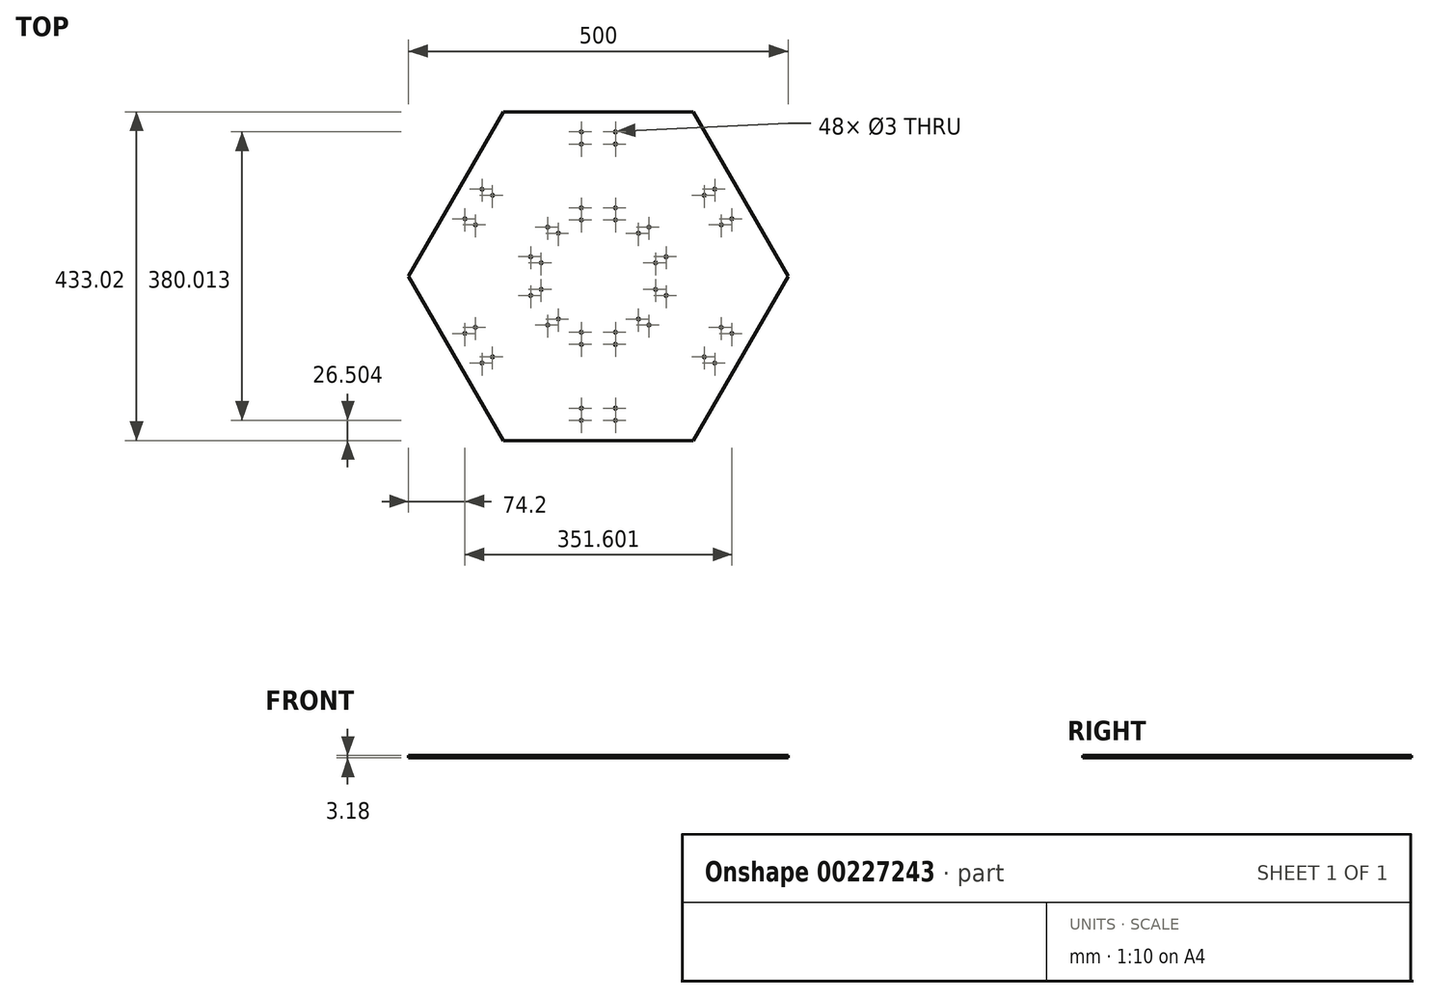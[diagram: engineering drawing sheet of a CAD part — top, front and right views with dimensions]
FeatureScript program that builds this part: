
annotation { "Feature Type Name" : "Feature", "Feature Type Description" : "" }
export const myFeature = defineFeature(function(context is Context, id is Id, definition is map)
    precondition{}
    {
        {
            var Q0;
            Q0=qCreatedBy(makeId("Top.planeOp"),FACE);
            var sketch = newSketch(context, id + "F0", { "sketchPlane" : qUnion([Q0])});
            skCircle(sketch, "E0.cCircle", {"center": v(0, 0) * mm, "radius": 250 * mm, "construction": true});
            skLineSegment(sketch, "E0.0", {"start": v(250, 0) * mm, "end": v(125, -216.5) * mm});
            skLineSegment(sketch, "E0.1", {"start": v(125, -216.5) * mm, "end": v(-125, -216.5) * mm});
            skLineSegment(sketch, "E0.2", {"start": v(-125, -216.5) * mm, "end": v(-250, 0) * mm});
            skLineSegment(sketch, "E0.3", {"start": v(-250, 0) * mm, "end": v(-125, 216.5) * mm});
            skLineSegment(sketch, "E0.4", {"start": v(-125, 216.5) * mm, "end": v(125, 216.5) * mm});
            skLineSegment(sketch, "E0.5", {"start": v(125, 216.5) * mm, "end": v(250, 0) * mm});
            skCircle(sketch, "E1", {"center": v(-22.5, 190) * mm, "radius": 1.5 * mm});
            skCircle(sketch, "E2.MirrorC", {"center": v(22.5, 190) * mm, "radius": 1.5 * mm});
            skCircle(sketch, "E3.0.1.0", {"center": v(-22.5, 174) * mm, "radius": 1.5 * mm});
            skCircle(sketch, "E3.0.1.1", {"center": v(22.5, 174) * mm, "radius": 1.5 * mm});
            skLineSegment(sketch, "E3.direction1", {"start": v(-22.5, 190) * mm, "end": v(2.5, 190) * mm, "construction": true});
            skLineSegment(sketch, "E3.direction2", {"start": v(-22.5, 190) * mm, "end": v(-22.5, 174) * mm, "construction": true});
            skCircle(sketch, "E4.0.1.0", {"center": v(22.5, 90) * mm, "radius": 1.5 * mm});
            skCircle(sketch, "E4.0.1.1", {"center": v(-22.5, 74) * mm, "radius": 1.5 * mm});
            skCircle(sketch, "E4.0.1.2", {"center": v(22.5, 74) * mm, "radius": 1.5 * mm});
            skLineSegment(sketch, "E4.0.1.3", {"start": v(-22.5, 90) * mm, "end": v(2.5, 90) * mm, "construction": true});
            skLineSegment(sketch, "E4.0.1.4", {"start": v(-22.5, 90) * mm, "end": v(-22.5, 74) * mm, "construction": true});
            skCircle(sketch, "E4.0.1.5", {"center": v(-22.5, 90) * mm, "radius": 1.5 * mm});
            skLineSegment(sketch, "E4.direction1", {"start": v(-22.5, 174) * mm, "end": v(2.5, 174) * mm, "construction": true});
            skLineSegment(sketch, "E4.direction2", {"start": v(-22.5, 174) * mm, "end": v(-22.5, 74) * mm, "construction": true});
            skLineSegment(sketch, "E5.1.0", {"start": v(-175.8, 75.52) * mm, "end": v(-163.3, 97.17) * mm, "construction": true});
            skLineSegment(sketch, "E5.1.1", {"start": v(-175.8, 75.52) * mm, "end": v(-161.94, 67.52) * mm, "construction": true});
            skLineSegment(sketch, "E5.1.2", {"start": v(-161.94, 67.52) * mm, "end": v(-75.34, 17.52) * mm, "construction": true});
            skLineSegment(sketch, "E5.1.3", {"start": v(-89.2, 25.52) * mm, "end": v(-76.7, 47.17) * mm, "construction": true});
            skLineSegment(sketch, "E5.1.4", {"start": v(-161.94, 67.52) * mm, "end": v(-149.44, 89.17) * mm, "construction": true});
            skCircle(sketch, "E5.1.5", {"center": v(-66.7, 64.49) * mm, "radius": 1.5 * mm});
            skLineSegment(sketch, "E5.1.6", {"start": v(-89.2, 25.52) * mm, "end": v(-75.34, 17.52) * mm, "construction": true});
            skCircle(sketch, "E5.1.7", {"center": v(-52.84, 56.49) * mm, "radius": 1.5 * mm});
            skCircle(sketch, "E5.1.8", {"center": v(-153.3, 114.49) * mm, "radius": 1.5 * mm});
            skCircle(sketch, "E5.1.9", {"center": v(-139.44, 106.49) * mm, "radius": 1.5 * mm});
            skCircle(sketch, "E5.1.10", {"center": v(-75.34, 17.52) * mm, "radius": 1.5 * mm});
            skCircle(sketch, "E5.1.11", {"center": v(-175.8, 75.52) * mm, "radius": 1.5 * mm});
            skCircle(sketch, "E5.1.12", {"center": v(-89.2, 25.52) * mm, "radius": 1.5 * mm});
            skCircle(sketch, "E5.1.13", {"center": v(-161.94, 67.52) * mm, "radius": 1.5 * mm});
            skLineSegment(sketch, "E5.2.0", {"start": v(-153.3, -114.49) * mm, "end": v(-165.8, -92.84) * mm, "construction": true});
            skLineSegment(sketch, "E5.2.1", {"start": v(-153.3, -114.49) * mm, "end": v(-139.44, -106.49) * mm, "construction": true});
            skLineSegment(sketch, "E5.2.2", {"start": v(-139.44, -106.49) * mm, "end": v(-52.84, -56.49) * mm, "construction": true});
            skLineSegment(sketch, "E5.2.3", {"start": v(-66.7, -64.49) * mm, "end": v(-79.2, -42.84) * mm, "construction": true});
            skLineSegment(sketch, "E5.2.4", {"start": v(-139.44, -106.49) * mm, "end": v(-151.94, -84.84) * mm, "construction": true});
            skCircle(sketch, "E5.2.5", {"center": v(-89.2, -25.52) * mm, "radius": 1.5 * mm});
            skLineSegment(sketch, "E5.2.6", {"start": v(-66.7, -64.49) * mm, "end": v(-52.84, -56.49) * mm, "construction": true});
            skCircle(sketch, "E5.2.7", {"center": v(-75.34, -17.52) * mm, "radius": 1.5 * mm});
            skCircle(sketch, "E5.2.8", {"center": v(-175.8, -75.52) * mm, "radius": 1.5 * mm});
            skCircle(sketch, "E5.2.9", {"center": v(-161.94, -67.52) * mm, "radius": 1.5 * mm});
            skCircle(sketch, "E5.2.10", {"center": v(-52.84, -56.49) * mm, "radius": 1.5 * mm});
            skCircle(sketch, "E5.2.11", {"center": v(-153.3, -114.49) * mm, "radius": 1.5 * mm});
            skCircle(sketch, "E5.2.12", {"center": v(-66.7, -64.49) * mm, "radius": 1.5 * mm});
            skCircle(sketch, "E5.2.13", {"center": v(-139.44, -106.49) * mm, "radius": 1.5 * mm});
            skLineSegment(sketch, "E5.3.0", {"start": v(22.5, -190) * mm, "end": v(-2.5, -190) * mm, "construction": true});
            skLineSegment(sketch, "E5.3.1", {"start": v(22.5, -190) * mm, "end": v(22.5, -174) * mm, "construction": true});
            skLineSegment(sketch, "E5.3.2", {"start": v(22.5, -174) * mm, "end": v(22.5, -74) * mm, "construction": true});
            skLineSegment(sketch, "E5.3.3", {"start": v(22.5, -90) * mm, "end": v(-2.5, -90) * mm, "construction": true});
            skLineSegment(sketch, "E5.3.4", {"start": v(22.5, -174) * mm, "end": v(-2.5, -174) * mm, "construction": true});
            skCircle(sketch, "E5.3.5", {"center": v(-22.5, -90) * mm, "radius": 1.5 * mm});
            skLineSegment(sketch, "E5.3.6", {"start": v(22.5, -90) * mm, "end": v(22.5, -74) * mm, "construction": true});
            skCircle(sketch, "E5.3.7", {"center": v(-22.5, -74) * mm, "radius": 1.5 * mm});
            skCircle(sketch, "E5.3.8", {"center": v(-22.5, -190) * mm, "radius": 1.5 * mm});
            skCircle(sketch, "E5.3.9", {"center": v(-22.5, -174) * mm, "radius": 1.5 * mm});
            skCircle(sketch, "E5.3.10", {"center": v(22.5, -74) * mm, "radius": 1.5 * mm});
            skCircle(sketch, "E5.3.11", {"center": v(22.5, -190) * mm, "radius": 1.5 * mm});
            skCircle(sketch, "E5.3.12", {"center": v(22.5, -90) * mm, "radius": 1.5 * mm});
            skCircle(sketch, "E5.3.13", {"center": v(22.5, -174) * mm, "radius": 1.5 * mm});
            skLineSegment(sketch, "E5.4.0", {"start": v(175.8, -75.52) * mm, "end": v(163.3, -97.17) * mm, "construction": true});
            skLineSegment(sketch, "E5.4.1", {"start": v(175.8, -75.52) * mm, "end": v(161.94, -67.52) * mm, "construction": true});
            skLineSegment(sketch, "E5.4.2", {"start": v(161.94, -67.52) * mm, "end": v(75.34, -17.52) * mm, "construction": true});
            skLineSegment(sketch, "E5.4.3", {"start": v(89.2, -25.52) * mm, "end": v(76.7, -47.17) * mm, "construction": true});
            skLineSegment(sketch, "E5.4.4", {"start": v(161.94, -67.52) * mm, "end": v(149.44, -89.17) * mm, "construction": true});
            skCircle(sketch, "E5.4.5", {"center": v(66.7, -64.49) * mm, "radius": 1.5 * mm});
            skLineSegment(sketch, "E5.4.6", {"start": v(89.2, -25.52) * mm, "end": v(75.34, -17.52) * mm, "construction": true});
            skCircle(sketch, "E5.4.7", {"center": v(52.84, -56.49) * mm, "radius": 1.5 * mm});
            skCircle(sketch, "E5.4.8", {"center": v(153.3, -114.49) * mm, "radius": 1.5 * mm});
            skCircle(sketch, "E5.4.9", {"center": v(139.44, -106.49) * mm, "radius": 1.5 * mm});
            skCircle(sketch, "E5.4.10", {"center": v(75.34, -17.52) * mm, "radius": 1.5 * mm});
            skCircle(sketch, "E5.4.11", {"center": v(175.8, -75.52) * mm, "radius": 1.5 * mm});
            skCircle(sketch, "E5.4.12", {"center": v(89.2, -25.52) * mm, "radius": 1.5 * mm});
            skCircle(sketch, "E5.4.13", {"center": v(161.94, -67.52) * mm, "radius": 1.5 * mm});
            skLineSegment(sketch, "E5.5.0", {"start": v(153.3, 114.49) * mm, "end": v(165.8, 92.84) * mm, "construction": true});
            skLineSegment(sketch, "E5.5.1", {"start": v(153.3, 114.49) * mm, "end": v(139.44, 106.49) * mm, "construction": true});
            skLineSegment(sketch, "E5.5.2", {"start": v(139.44, 106.49) * mm, "end": v(52.84, 56.49) * mm, "construction": true});
            skLineSegment(sketch, "E5.5.3", {"start": v(66.7, 64.49) * mm, "end": v(79.2, 42.84) * mm, "construction": true});
            skLineSegment(sketch, "E5.5.4", {"start": v(139.44, 106.49) * mm, "end": v(151.94, 84.84) * mm, "construction": true});
            skCircle(sketch, "E5.5.5", {"center": v(89.2, 25.52) * mm, "radius": 1.5 * mm});
            skLineSegment(sketch, "E5.5.6", {"start": v(66.7, 64.49) * mm, "end": v(52.84, 56.49) * mm, "construction": true});
            skCircle(sketch, "E5.5.7", {"center": v(75.34, 17.52) * mm, "radius": 1.5 * mm});
            skCircle(sketch, "E5.5.8", {"center": v(175.8, 75.52) * mm, "radius": 1.5 * mm});
            skCircle(sketch, "E5.5.9", {"center": v(161.94, 67.52) * mm, "radius": 1.5 * mm});
            skCircle(sketch, "E5.5.10", {"center": v(52.84, 56.49) * mm, "radius": 1.5 * mm});
            skCircle(sketch, "E5.5.11", {"center": v(153.3, 114.49) * mm, "radius": 1.5 * mm});
            skCircle(sketch, "E5.5.12", {"center": v(66.7, 64.49) * mm, "radius": 1.5 * mm});
            skCircle(sketch, "E5.5.13", {"center": v(139.44, 106.49) * mm, "radius": 1.5 * mm});
            skSolve(sketch);
        }
        {
            var Q0;
            Q0=makeQuery(id+"F0.imprint","IMPRINT",FACE,{"disambiguationData":[TD([[makeQuery(id+"F0.imprint","IMPRINT",EDGE,{"derivedFrom":sQuery(id+"F0.wireOp",EDGE,"E0.0")}),-1.0]])]});
            extrude(context, id + "F1", {"entities" : qUnion([Q0]), "depth" : 3.17 * mm});
        }
    });
